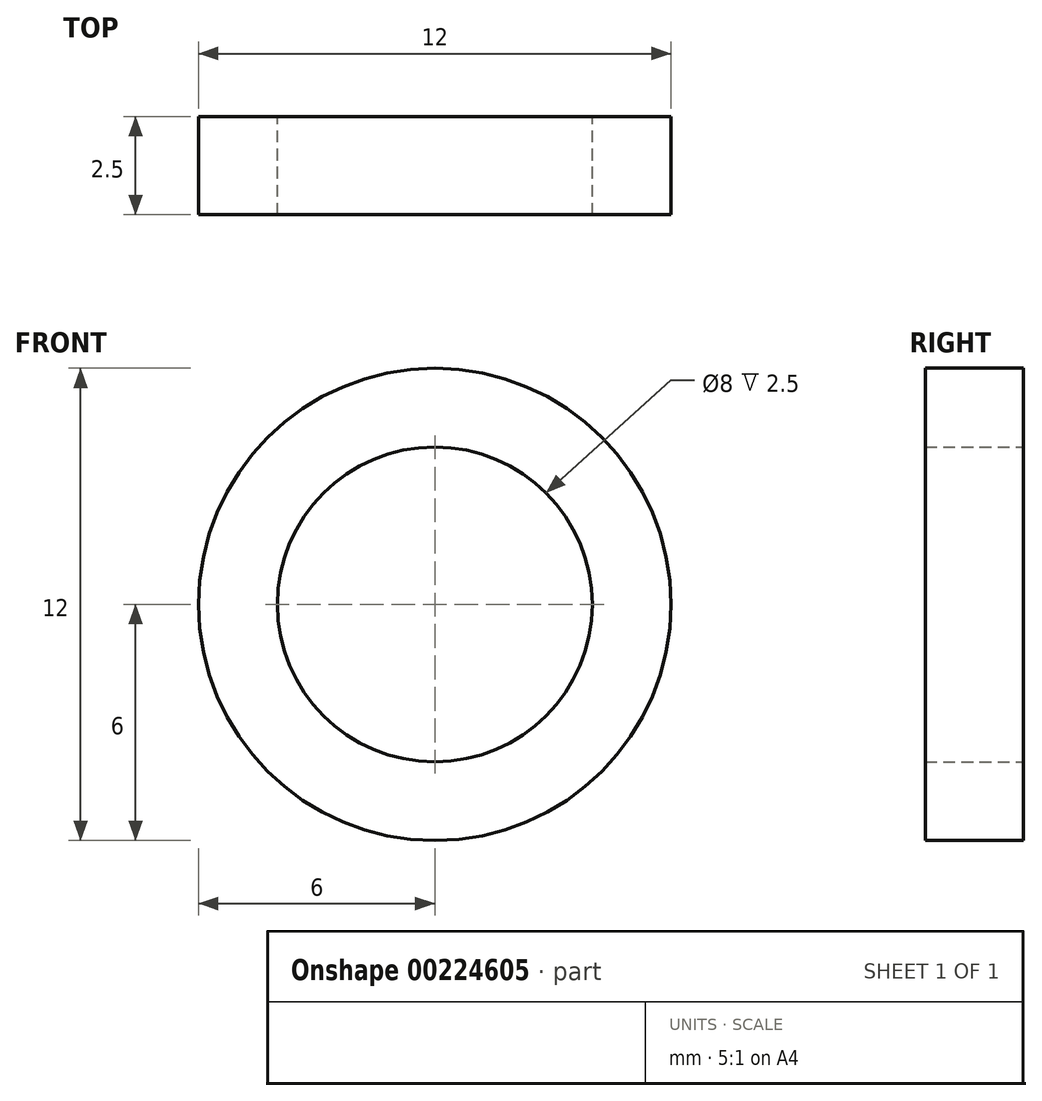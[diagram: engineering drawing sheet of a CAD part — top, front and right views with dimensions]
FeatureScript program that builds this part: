
annotation { "Feature Type Name" : "Feature", "Feature Type Description" : "" }
export const myFeature = defineFeature(function(context is Context, id is Id, definition is map)
    precondition{}
    {
        {
            var Q0;
            Q0=qCreatedBy(makeId("Front.planeOp"),FACE);
            var sketch = newSketch(context, id + "F0", { "sketchPlane" : qUnion([Q0])});
            skCircle(sketch, "E0", {"center": v(0, 0) * mm, "radius": 6 * mm});
            skCircle(sketch, "E1", {"center": v(0, 0) * mm, "radius": 4 * mm});
            skSolve(sketch);
        }
        {
            var Q0;
            Q0 = qSketchRegion(id + "F0", true);
            extrude(context, id + "F1", {"entities" : qUnion([Q0]), "depth" : 2.5 * mm});
        }
    });
